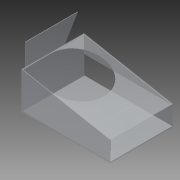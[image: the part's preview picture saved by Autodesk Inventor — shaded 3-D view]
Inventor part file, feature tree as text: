
AUTODESK INVENTOR PART (.ipt)
format: ipt  version: 2013 (Build 170138000, 138)  size: 203,776 bytes
history: native  units: in
note: dims shown in document units (in); Inventor stores cm internally (conversion verified against a paired STEP export)
features: extrude x11, sketch x11
ambient origin geometry x8: Origin, YZ Plane, XZ Plane, XY Plane, X Axis, Y Axis, Z Axis, Center Point
bodies: Solid1 (feature_tree)
feature tree (22):
  extrude  "Extrusion1"  Depth=0.125in TaperAngle=0.0deg
  extrude  "Extrusion2"  TaperAngle=90.0deg  [1 undecoded]
  extrude  "Extrusion3"  Depth=0.125in TaperAngle=0.0deg
  extrude  "Extrusion4"  Depth=13.0in
  extrude  "Extrusion5"  Depth=0.125in TaperAngle=0.0deg
  extrude  "Extrusion6"  Depth=0.125in TaperAngle=0.0deg
  extrude  "Extrusion7"  Depth=0.125in TaperAngle=0.0deg
  extrude  "Extrusion8"  Depth=11.5in
  extrude  "Extrusion9"  Depth=6.0in
  extrude  "Extrusion10"  Depth=5.0in
  extrude  "Extrusion11"  TaperAngle=0.0deg  [1 undecoded]
  sketch  "Sketch1"  dims[d0=3.5in d2=0.125in d3=0.0in]
  sketch  "Sketch2"  dims[d4=18.75in d5=90.0deg]
  sketch  "Sketch3"  dims[d6=13.0in d7=0.125in d8=0.0in]
  sketch  "Sketch4"  dims[d9=0.125in d10=13.0in]
  sketch  "Sketch5"  dims[d11=4.0in d12=0.125in d13=0.0in]
  sketch  "Sketch6"  dims[d14=13.0in d15=0.0in d16=0.125in d17=0.0in]
  sketch  "Sketch7"  dims[d18=13.0in d19=0.0in d20=0.125in d21=0.0in]
  sketch  "Sketch8"  dims[d22=0.125in d23=0.0in d24=11.5in]
  sketch  "Sketch9"  dims[d28=0.125in d29=0.0in d30=6.0in]
  sketch  "Sketch10"  dims[d31=8.0in d32=5.0in]
  sketch  "Sketch11"  dims[d33=2.0in d34=0.0in d35=0.0in d37=0.125in d38=0.0in d39=11.0in d40=6.5in d41=8.25in d42=2.0in d43=0.0in d44=0.875in d45=0.125in d46=0.0in d47=0.0in]
note: 2 required parameter values undecoded (feature->parameter linkage not recoverable at this tier; creation-order binding heuristic only, values carry confidence <= 0.55)
